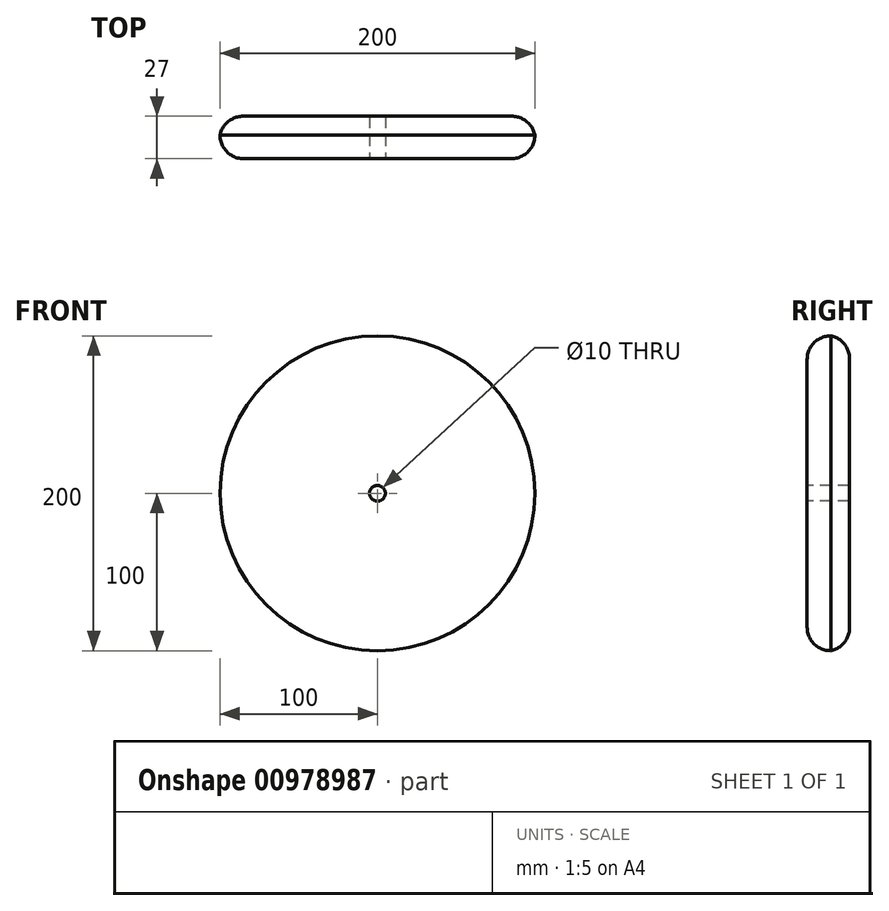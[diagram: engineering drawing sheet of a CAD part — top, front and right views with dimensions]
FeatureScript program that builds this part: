
annotation { "Feature Type Name" : "Feature", "Feature Type Description" : "" }
export const myFeature = defineFeature(function(context is Context, id is Id, definition is map)
    precondition{}
    {
        {
            var Q0;
            Q0=qCreatedBy(makeId("Front.planeOp"),FACE);
            var sketch = newSketch(context, id + "F0", { "sketchPlane" : qUnion([Q0])});
            skCircle(sketch, "E0", {"center": v(0, 0) * mm, "radius": 100 * mm});
            skSolve(sketch);
        }
        {
            var Q0;
            Q0=makeQuery(id+"F0.imprint","IMPRINT",FACE,{"disambiguationData":[TD([[makeQuery(id+"F0.imprint","IMPRINT",EDGE,{"derivedFrom":sQuery(id+"F0.wireOp",EDGE,"E0")}),1.0]])]});
            extrude(context, id + "F1", {"entities" : qUnion([Q0]), "depth" : 27 * mm, "offsetDistance" : 25 * mm});
        }
        {
            var Q0;
            Q0=makeQuery(id+"F1.opExtrude","CAP_EDGE",EDGE,{"disambiguationData":[OSD([sQuery(id+"F0.wireOp",EDGE,"E0")])],"isStart":false});
            fillet(context, id + "F2", {"entities" : qUnion([Q0]), "radius" : 15 * mm, "tangentPropagation" : true, "allowEdgeOverflow" : false});
        }
        {
            var Q0;
            Q0=makeQuery(id+"F1.opExtrude","CAP_EDGE",EDGE,{"disambiguationData":[OSD([sQuery(id+"F0.wireOp",EDGE,"E0")])],"isStart":true});
            fillet(context, id + "F3", {"entities" : qUnion([Q0]), "radius" : 15 * mm, "tangentPropagation" : true, "allowEdgeOverflow" : false});
        }
        {
            var Q0;
            Q0=makeQuery(id+"F1.opExtrude","CAP_FACE",FACE,{"disambiguationData":[OSD([sQuery(id+"F0.wireOp",EDGE,"E0")])],"isStart":false});
            var sketch = newSketch(context, id + "F4", { "sketchPlane" : qUnion([Q0])});
            skCircle(sketch, "E1", {"center": v(0, 0) * mm, "radius": 5 * mm});
            skSolve(sketch);
        }
        {
            var Q0;
            Q0=makeQuery(id+"F4.imprint","IMPRINT",FACE,{"disambiguationData":[TD([[makeQuery(id+"F4.imprint","IMPRINT",EDGE,{"derivedFrom":sQuery(id+"F4.wireOp",EDGE,"E1")}),1.0]])]});
            var Q1;
            Q1=sQuery(id+"F4.wireOp",EDGE,"E1");
            extrude(context, id + "F5", {"entities" : qUnion([Q0]), "operationType" : NewBodyOperationType.REMOVE, "surfaceEntities" : qUnion([Q1]), "oppositeDirection" : true, "depth" : 30 * mm, "offsetDistance" : 25 * mm});
        }
    });
